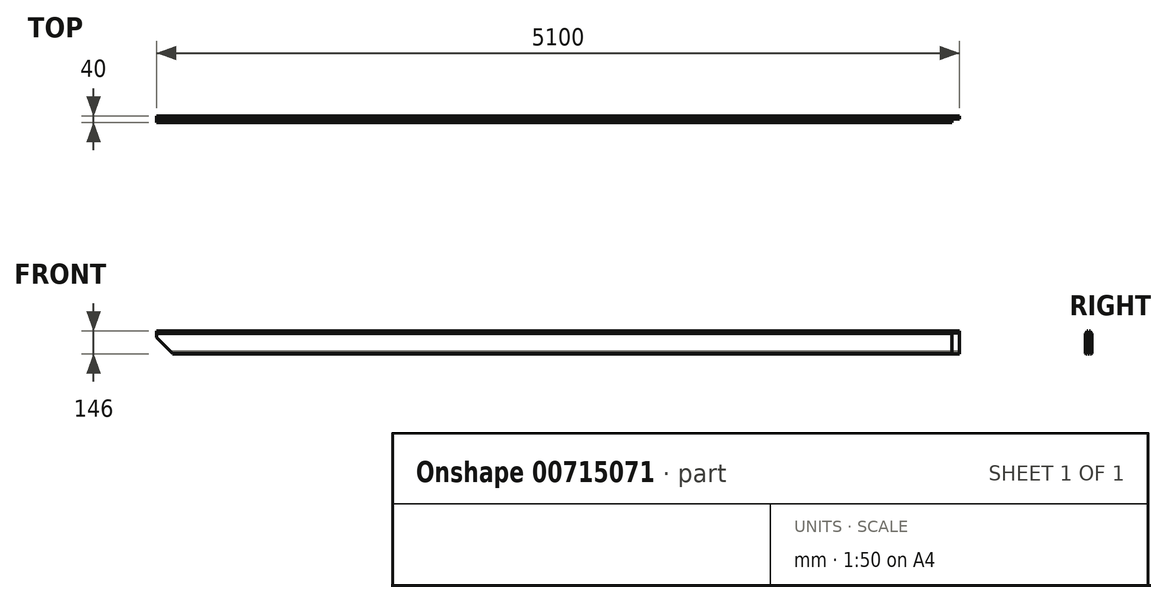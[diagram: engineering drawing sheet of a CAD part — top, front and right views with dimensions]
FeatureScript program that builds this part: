
annotation { "Feature Type Name" : "Feature", "Feature Type Description" : "" }
export const myFeature = defineFeature(function(context is Context, id is Id, definition is map)
    precondition{}
    {
        {
            var Q0;
            Q0=qCreatedBy(makeId("Right.planeOp"),FACE);
            var sketch = newSketch(context, id + "F0", { "sketchPlane" : qUnion([Q0])});
            skLineSegment(sketch, "E0", {"start": v(20, 56) * mm, "end": v(20, -70) * mm});
            skLineSegment(sketch, "E1", {"start": v(20, -70) * mm, "end": v(17, -73) * mm});
            skLineSegment(sketch, "E2", {"start": v(17, -73) * mm, "end": v(12, -73) * mm});
            skLineSegment(sketch, "E3", {"start": v(12, -59) * mm, "end": v(12, -73) * mm});
            skLineSegment(sketch, "E4", {"start": v(12, -59) * mm, "end": v(4, -59) * mm});
            skLineSegment(sketch, "E5", {"start": v(4, -73) * mm, "end": v(4, -59) * mm});
            skLineSegment(sketch, "E6", {"start": v(4, -73) * mm, "end": v(-4, -73) * mm});
            skLineSegment(sketch, "E7", {"start": v(-4, -59) * mm, "end": v(-4, -73) * mm});
            skLineSegment(sketch, "E8", {"start": v(-4, -59) * mm, "end": v(-12, -59) * mm});
            skLineSegment(sketch, "E9", {"start": v(-12, -73) * mm, "end": v(-12, -59) * mm});
            skLineSegment(sketch, "E10", {"start": v(-12, -73) * mm, "end": v(-17, -73) * mm});
            skLineSegment(sketch, "E11", {"start": v(-17, -73) * mm, "end": v(-20, -70) * mm});
            skLineSegment(sketch, "E12", {"start": v(-20, -70) * mm, "end": v(-20, 56) * mm});
            skLineSegment(sketch, "E13", {"start": v(-20, 56) * mm, "end": v(-17, 59) * mm});
            skLineSegment(sketch, "E14", {"start": v(-17, 59) * mm, "end": v(-12, 59) * mm});
            skLineSegment(sketch, "E15", {"start": v(-4, 59) * mm, "end": v(4, 59) * mm});
            skLineSegment(sketch, "E16", {"start": v(12, 59) * mm, "end": v(17, 59) * mm});
            skLineSegment(sketch, "E17", {"start": v(17, 59) * mm, "end": v(20, 56) * mm});
            skPoint(sketch, "E18.end.orphan", {"position": v(12, 57.8) * mm});
            skPoint(sketch, "E19.end.orphan", {"position": v(4, 66.3) * mm});
            skPoint(sketch, "E20.end.orphan", {"position": v(-4, 66.3) * mm});
            skLineSegment(sketch, "E21", {"start": v(-12, 59) * mm, "end": v(-12, 73) * mm});
            skLineSegment(sketch, "E22", {"start": v(-12, 73) * mm, "end": v(-4, 73) * mm});
            skLineSegment(sketch, "E23", {"start": v(-4, 73) * mm, "end": v(-4, 59) * mm});
            skLineSegment(sketch, "E24", {"start": v(4, 59) * mm, "end": v(4, 73) * mm});
            skLineSegment(sketch, "E25", {"start": v(4, 73) * mm, "end": v(12, 73) * mm});
            skLineSegment(sketch, "E26", {"start": v(12, 73) * mm, "end": v(12, 59) * mm});
            skSolve(sketch);
        }
        {
            var Q0;
            Q0=makeQuery(id+"F0.imprint","IMPRINT",FACE,{"disambiguationData":[TD([[makeQuery(id+"F0.imprint","IMPRINT",EDGE,{"derivedFrom":sQuery(id+"F0.wireOp",EDGE,"E0")}),-1.0]])]});
            extrude(context, id + "F1", {"entities" : qUnion([Q0]), "endBound" : BoundingType.SYMMETRIC, "depth" : 5100 * mm, "offsetDistance" : 25 * mm});
        }
        {
            var Q0;
            Q0=qCreatedBy(makeId("Front.planeOp"),FACE);
            var sketch = newSketch(context, id + "F2", { "sketchPlane" : qUnion([Q0])});
            skLineSegment(sketch, "E27", {"start": v(-2566.78, 47) * mm, "end": v(-2390, -129.78) * mm});
            skLineSegment(sketch, "E28", {"start": v(-2566.78, 47) * mm, "end": v(-2566.78, -129.78) * mm});
            skLineSegment(sketch, "E29", {"start": v(-2566.78, -129.78) * mm, "end": v(-2390, -129.78) * mm});
            skSolve(sketch);
        }
        {
            var Q0;
            Q0=makeQuery(id+"F2.imprint","IMPRINT",FACE,{"disambiguationData":[TD([[makeQuery(id+"F2.imprint","IMPRINT",EDGE,{"derivedFrom":sQuery(id+"F2.wireOp",EDGE,"E27")}),-1.0]])]});
            extrude(context, id + "F3", {"entities" : qUnion([Q0]), "operationType" : NewBodyOperationType.REMOVE, "endBound" : BoundingType.SYMMETRIC, "oppositeDirection" : true, "depth" : 50 * mm, "offsetDistance" : 25 * mm});
        }
        {
            var Q0;
            Q0=makeQuery(id+"F1.opExtrude","CAP_FACE",FACE,{"disambiguationData":[OSD([sQuery(id+"F0.wireOp",EDGE,"E0"),sQuery(id+"F0.wireOp",EDGE,"E1"),sQuery(id+"F0.wireOp",EDGE,"E2"),sQuery(id+"F0.wireOp",EDGE,"E3"),sQuery(id+"F0.wireOp",EDGE,"E4"),sQuery(id+"F0.wireOp",EDGE,"E5"),sQuery(id+"F0.wireOp",EDGE,"E6"),sQuery(id+"F0.wireOp",EDGE,"E7"),sQuery(id+"F0.wireOp",EDGE,"E8"),sQuery(id+"F0.wireOp",EDGE,"E9"),sQuery(id+"F0.wireOp",EDGE,"E10"),sQuery(id+"F0.wireOp",EDGE,"E11"),sQuery(id+"F0.wireOp",EDGE,"E12"),sQuery(id+"F0.wireOp",EDGE,"E13"),sQuery(id+"F0.wireOp",EDGE,"E14"),sQuery(id+"F0.wireOp",EDGE,"E15"),sQuery(id+"F0.wireOp",EDGE,"E16"),sQuery(id+"F0.wireOp",EDGE,"E17"),sQuery(id+"F0.wireOp",EDGE,"E21"),sQuery(id+"F0.wireOp",EDGE,"E22"),sQuery(id+"F0.wireOp",EDGE,"E23"),sQuery(id+"F0.wireOp",EDGE,"E24"),sQuery(id+"F0.wireOp",EDGE,"E25"),sQuery(id+"F0.wireOp",EDGE,"E26")])],"isStart":false});
            var sketch = newSketch(context, id + "F4", { "sketchPlane" : qUnion([Q0])});
            skLineSegment(sketch, "E30.bottom", {"start": v(0, -95.08) * mm, "end": v(-40, -95.08) * mm});
            skLineSegment(sketch, "E30.top", {"start": v(0, 81.08) * mm, "end": v(-40, 81.08) * mm});
            skLineSegment(sketch, "E30.left", {"start": v(0, -95.08) * mm, "end": v(0, 81.08) * mm});
            skLineSegment(sketch, "E30.right", {"start": v(-40, -95.08) * mm, "end": v(-40, 81.08) * mm});
            skPoint(sketch, "E30.middle", {"position": v(-20, -7) * mm});
            skSolve(sketch);
        }
        {
            var Q0;
            {var subQ0=makeQuery(id+"F1.opExtrude","CAP_EDGE",EDGE,{"disambiguationData":[OSD([sQuery(id+"F0.wireOp",EDGE,"E7")])],"isStart":false});Q0=makeQuery(id+"F4.imprint","IMPRINT",FACE,{"disambiguationData":[TD([[makeQuery(id+"F4.imprint","IMPRINT",EDGE,{"derivedFrom":subQ0}),1.0]])]});}
            extrude(context, id + "F5", {"entities" : qUnion([Q0]), "operationType" : NewBodyOperationType.REMOVE, "oppositeDirection" : true, "depth" : 50 * mm, "offsetDistance" : 25 * mm});
        }
    });
